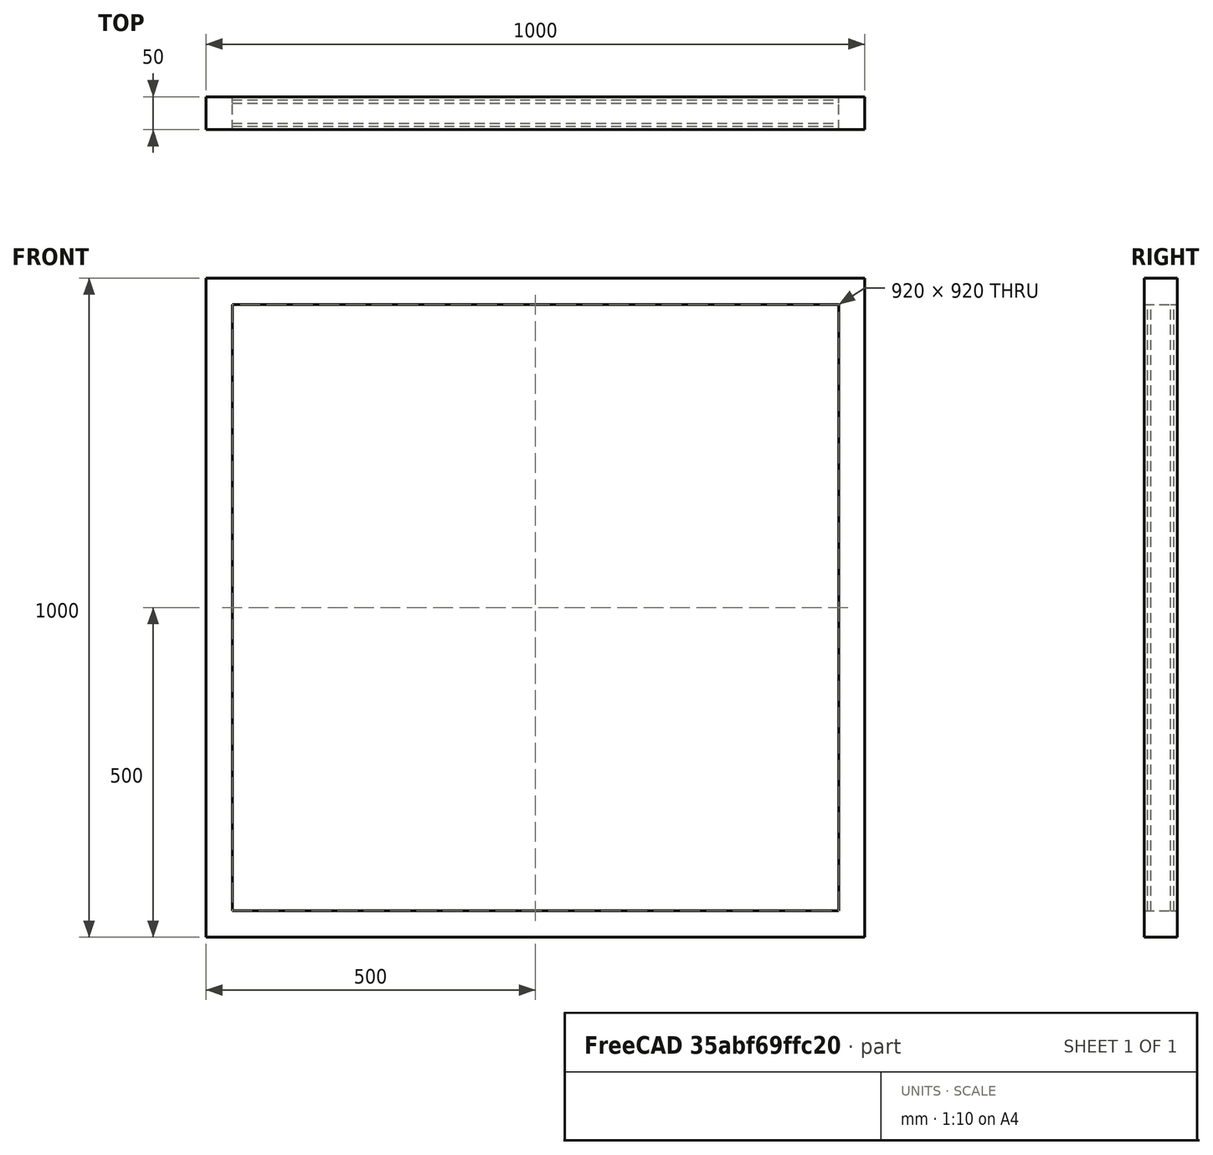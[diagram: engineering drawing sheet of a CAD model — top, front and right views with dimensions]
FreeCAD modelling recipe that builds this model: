
FCSTD DOCUMENT  (FreeCAD 0.16R6704 (Git))
Label: Window fixed double glazed windows with shutters
License: CreativeCommons Attribution
LicenseURL: http://creativecommons.org/licenses/by/4.0/
objects: Sketcher::SketchObject×2, Part::FeaturePython×2, Part::Extrusion×1, App::DocumentObjectGroup×1
note: 5 computed .brp shape members not serialized (recipe doc carries the construction recipe); baked Part::Feature solids carry a one-line shape summary decoded from their .brp

FEATURE [Sketcher::SketchObject] Sketch092  label="Esboco_janela_persiana"
  Placement = pos=(0,0,0) rot=(1,0,0;1.5708rad)
  sketch-geometry (12):
    g0: LineSegment StartX=0 StartY=0 StartZ=0 EndX=1000 EndY=0 EndZ=0
    g1: LineSegment StartX=1000 StartY=0 StartZ=0 EndX=1000 EndY=1000 EndZ=0
    g2: LineSegment StartX=1000 StartY=1000 StartZ=0 EndX=0 EndY=1000 EndZ=0
    g3: LineSegment StartX=0 StartY=1000 StartZ=0 EndX=0 EndY=0 EndZ=0
    g4: LineSegment StartX=40 StartY=40 StartZ=0 EndX=960 EndY=40 EndZ=0
    g5: LineSegment StartX=960 StartY=40 StartZ=0 EndX=960 EndY=960 EndZ=0
    g6: LineSegment StartX=960 StartY=960 StartZ=0 EndX=40 EndY=960 EndZ=0
    g7: LineSegment StartX=40 StartY=960 StartZ=0 EndX=40 EndY=40 EndZ=0
    g8: LineSegment [constr] StartX=329.495 StartY=1000 StartZ=0 EndX=329.495 EndY=960 EndZ=0
    g9: LineSegment [constr] StartX=0 StartY=730.903 StartZ=0 EndX=40 EndY=730.903 EndZ=0
    g10: LineSegment [constr] StartX=960 StartY=653.338 StartZ=0 EndX=1000 EndY=653.338 EndZ=0
    g11: LineSegment [constr] StartX=865.301 StartY=40 StartZ=0 EndX=865.301 EndY=0 EndZ=0
  constraints (35):
    c: Coincident(g0,g1)
    c: Coincident(g1,g2)
    c: Coincident(g2,g3)
    c: Coincident(g3,g0)
    c: Horizontal(g0)
    c: Horizontal(g2)
    c: Vertical(g1)
    c: Vertical(g3)
    c: Coincident(g4,g5)
    c: Coincident(g5,g6)
    c: Coincident(g6,g7)
    c: Coincident(g7,g4)
    c: Horizontal(g4)
    c: Horizontal(g6)
    c: Vertical(g5)
    c: Vertical(g7)
    c: DistanceY(g1) = 1000  'Altura_vao'
    c: DistanceX(g0) = 1000  'Largura_vao'
    c: DistanceX(g2,g6) = 40  'Perfis_montantes'
    c: Coincident(g0,g-1)
    c: PointOnObject(g8,g2)
    c: PointOnObject(g8,g6)
    c: PointOnObject(g9,g3)
    c: PointOnObject(g9,g7)
    c: PointOnObject(g10,g5)
    c: PointOnObject(g10,g1)
    c: PointOnObject(g11,g4)
    c: PointOnObject(g11,g0)
    c: Equal(g8,g9)
    c: Equal(g9,g10)
    c: Equal(g10,g11)
    c: Angle(g8) = -1.5708
    c: Angle(g9) = 0
    c: Angle(g10) = 0
    c: Angle(g11) = -1.5708
FEATURE [Part::FeaturePython] Window072  label="Window fixed double glazed windows with blind "  # WARN: FeaturePython — macro-defined, semantics opaque (R4)
  Base = -> Sketch092
  Height = 1000
  HoleDepth = 0
  MoveWithHost = true
  Normal = (0,1,0)
  Preset = 1
  Role = 0
  Width = 1000
  WindowParts = MONTANTES | Frame | Wire0,Wire1 | 50.0 | 0.0 | VIDRO 1 | Glass panel | Wire1 | 5.0 | 5.0 | VIDRO 2 | Glass panel | Wire1 | 5.0 | 40.0
FEATURE [Sketcher::SketchObject] Sketch093
  ExternalGeometry = -> [Window072]
  Placement = pos=(40,0,0) rot=(0.57735,0.57735,0.57735;2.0944rad)
  Support = -> Window072 [Face8]
  sketch-geometry (3):
    g0: LineSegment [constr] StartX=25 StartY=1022.15 StartZ=0 EndX=25 EndY=-15134 EndZ=0
    g1: ArcOfCircle CenterX=25 CenterY=937 CenterZ=0 NormalX=0 NormalY=0 NormalZ=1 Radius=7 StartAngle=4.71239 EndAngle=7.85398
    g2: ArcOfCircle CenterX=25 CenterY=951 CenterZ=0 NormalX=0 NormalY=0 NormalZ=1 Radius=7 StartAngle=1.5708 EndAngle=4.71239
  constraints (11):
    c: Symmetric(g-3,g-4,g0)
    c: PointOnObject(g1,g0)
    c: PointOnObject(g1,g0)
    c: PointOnObject(g1,g0)
    c: PointOnObject(g2,g0)
    c: PointOnObject(g2,g0)
    c: PointOnObject(g2,g0)
    c: Coincident(g2,g1)
    c: DistanceY(g1,g1) = 14
    c: DistanceY(g1,g2) = 14
    c: DistanceY(g2,g-5) = 2
FEATURE [Part::Extrusion] Extrude_Sketch093  label="Módulo persiana 001"
  Base = -> Sketch093
  Dir = (920,0,0)
  Solid = true
  expr: Dir.x = Esboco_janela_persiana.Constraints.Largura_vao - 2 * Esboco_janela_persiana.Constraints.Perfis_montantes
FEATURE [Part::FeaturePython] Array005  label="Internal blind "  # Draft array (typed FeaturePython)
  Angle = 360
  ArrayType = 0
  Axis = (0,0,1)
  Base = -> Extrude_Sketch093
  Center = (0,0,0)
  Fuse = false
  IntervalAxis = (0,0,0)
  IntervalX = (1,0,0)
  IntervalY = (0,1,0)
  IntervalZ = (0,0,-28)
  NumberPolar = 1
  NumberX = 1
  NumberY = 1
  NumberZ = 33
  expr: NumberZ = (Esboco_janela_persiana.Constraints.Altura_vao - 2 * Esboco_janela_persiana.Constraints.Perfis_montantes) / 28
FEATURE [App::DocumentObjectGroup] Grupo080  label="Window fixed double glazed windows with blind"
  Group = -> [Window072,Extrude_Sketch093,Array005]
